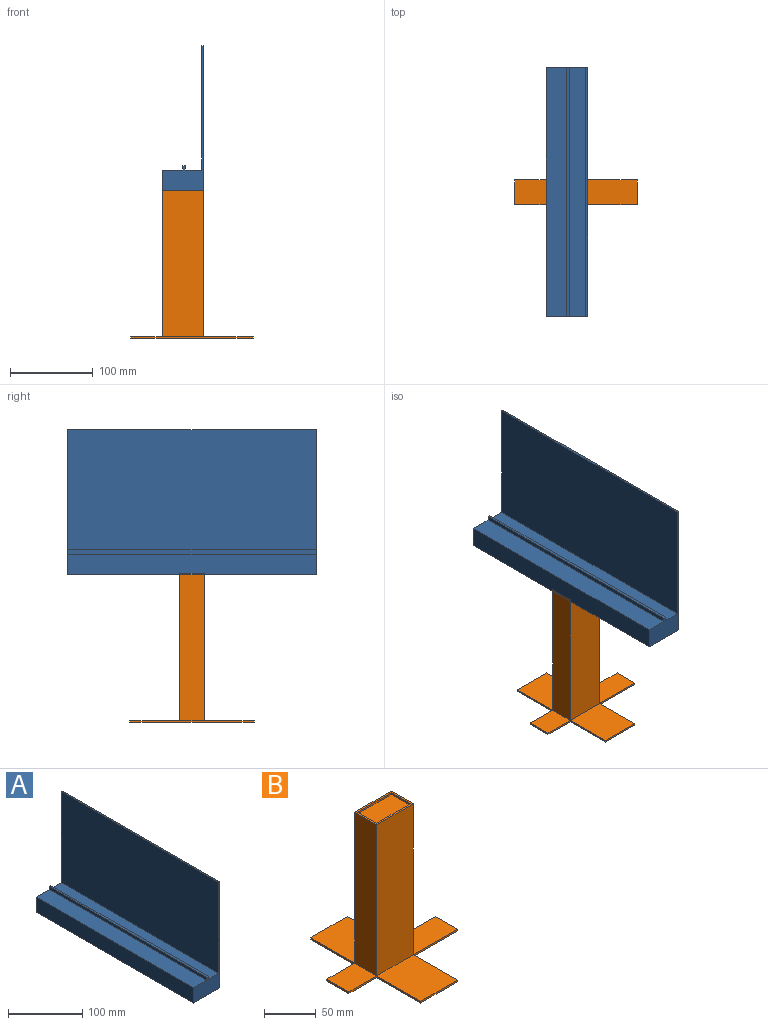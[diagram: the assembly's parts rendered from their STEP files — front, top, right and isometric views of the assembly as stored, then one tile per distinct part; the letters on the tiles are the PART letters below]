
ASSEMBLY  parts=2 mates=1
PART A: 17 faces, bbox 50x300x177 mm
  f0: plane 300x20mm, normal (0,0,1), area 6000mm2, adj f3,f6,f12,f14
  f1: plane 300x50mm, normal (0,0,-1), area 13804mm2, adj f2,f3,f4,f6,f7,f8,f9,f10
  f2: plane 300x175mm, normal (1,0,0), area 52500mm2, adj f1,f3,f6,f13
  f3: plane 175x50mm, normal (0,1,0), area 1565mm2, adj f0,f1,f2,f4,f5,f12,f13,f14
  f4: plane 300x25mm, normal (-1,0,0), area 7500mm2, adj f1,f3,f5,f6
  f5: plane 300x25mm, normal (0,0,1), area 7500mm2, adj f3,f4,f6,f15
  f6: plane 175x50mm, normal (0,-1,0), area 1565mm2, adj f0,f1,f2,f4,f5,f12,f13,f14
  f7: plane 46x2mm, normal (0,1,0), area 92mm2, adj f1,f8,f10,f11
  f8: plane 26x2mm, normal (-1,0,0), area 52mm2, adj f1,f7,f9,f11
  f9: plane 46x2mm, normal (0,-1,0), area 92mm2, adj f1,f8,f10,f11
  f10: plane 26x2mm, normal (1,0,0), area 52mm2, adj f1,f7,f9,f11
  f11: plane 46x26mm, normal (0,0,-1), area 1196mm2, adj f7,f8,f9,f10
  f12: plane 300x150mm, normal (-1,0,0), area 45000mm2, adj f0,f3,f6,f13
  f13: plane 300x2mm, normal (0,0,1), area 600mm2, adj f2,f3,f6,f12
  f14: plane 300x5mm, normal (1,0,0), area 1500mm2, adj f0,f3,f6,f16
  f15: plane 300x5mm, normal (-1,0,0), area 1500mm2, adj f3,f5,f6,f16
  f16: plane 300x3mm, normal (0,0,1), area 900mm2, adj f3,f6,f14,f15
PART B: 27 faces, bbox 147.8x150x180 mm
  f0: plane 50x30mm, normal (0,0,1), area 304mm2, adj f4,f6,f7,f8,f22,f23,f24,f25
  f1: plane 37.79x2mm, normal (0,-1,0), area 75.6mm2, adj f9,f12,f13,f19
  f2: plane 60x2mm, normal (0,-1,0), area 120mm2, adj f9,f10,f11,f18
  f3: plane 60x2mm, normal (0,1,0), area 120mm2, adj f9,f10,f11,f14
  f4: plane 178x50mm, normal (0,1,0), area 8900mm2, adj f0,f6,f8,f17
  f5: plane 37.79x2mm, normal (0,1,0), area 75.6mm2, adj f9,f12,f13,f16
  f6: plane 178x30mm, normal (-1,0,0), area 5340mm2, adj f0,f4,f7,f13
  f7: plane 178x50mm, normal (0,-1,0), area 8900mm2, adj f0,f6,f8,f21
  f8: plane 178x30mm, normal (1,0,0), area 5340mm2, adj f0,f4,f7,f11
  f9: plane 150x147.79mm, normal (0,0,-1), area 10433.6mm2, adj f1,f2,f3,f5,f10,f12,f14,f15
  f10: plane 30x2mm, normal (1,0,0), area 60mm2, adj f2,f3,f9,f11
  f11: plane 60x30mm, normal (0,0,1), area 1800mm2, adj f2,f3,f8,f10
  f12: plane 30x2mm, normal (-1,0,0), area 60mm2, adj f1,f5,f9,f13
  f13: plane 37.79x30mm, normal (0,0,1), area 1133.6mm2, adj f1,f5,f6,f12
  f14: plane 60x2mm, normal (1,0,0), area 120mm2, adj f3,f9,f15,f17
  f15: plane 50x2mm, normal (0,1,0), area 100mm2, adj f9,f14,f16,f17
  f16: plane 60x2mm, normal (-1,0,0), area 120mm2, adj f5,f9,f15,f17
  f17: plane 60x50mm, normal (0,0,1), area 3000mm2, adj f4,f14,f15,f16
  f18: plane 60x2mm, normal (1,0,0), area 120mm2, adj f2,f9,f20,f21
  f19: plane 60x2mm, normal (-1,0,0), area 120mm2, adj f1,f9,f20,f21
  f20: plane 50x2mm, normal (0,-1,0), area 100mm2, adj f9,f18,f19,f21
  f21: plane 60x50mm, normal (0,0,1), area 3000mm2, adj f7,f18,f19,f20
  f22: plane 26x2mm, normal (-1,0,0), area 52mm2, adj f0,f23,f25,f26
  f23: plane 46x2mm, normal (0,-1,0), area 92mm2, adj f0,f22,f24,f26
  f24: plane 26x2mm, normal (1,0,0), area 52mm2, adj f0,f23,f25,f26
  f25: plane 46x2mm, normal (0,1,0), area 92mm2, adj f0,f22,f24,f26
  f26: plane 46x26mm, normal (0,0,1), area 1196mm2, adj f22,f23,f24,f25
PLACE A t=(117.33,0,178)mm
PLACE B at identity
MATE fastened A.f1 <-> B.f26  axis (0,0,-1) through (0,0,178)mm
